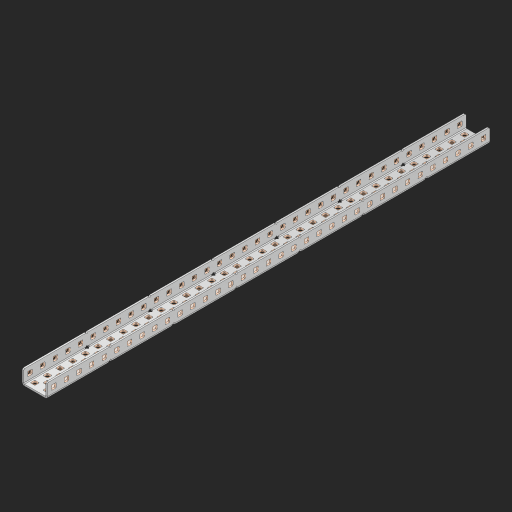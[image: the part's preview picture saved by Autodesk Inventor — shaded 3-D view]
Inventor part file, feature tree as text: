
AUTODESK INVENTOR PART (.ipt)
format: ipt  version: 2023 (Build 270158000, 158)  size: 2,018,816 bytes
history: native  units: in
note: dims shown in document units (in); Inventor stores cm internally (conversion verified against a paired STEP export)
features: other x322, extrude x172, sheet_metal_op x11, sketch x10, pattern_linear x2, mirror x1, chamfer x1
ambient origin geometry x8: Origin, YZ Plane, XZ Plane, XY Plane, X Axis, Y Axis, Z Axis, Center Point
bodies: Solid1 (feature_tree), Body (feature_tree)
feature tree (519):
  other  "Table"
  other  "Alu C 1x2x1x35"
  other  "Alu C 1x2x1x34"
  other  "Alu C 1x2x1x33"
  other  "Alu C 1x2x1x32"
  other  "Alu C 1x2x1x31"
  other  "Alu C 1x2x1x30"
  other  "Alu C 1x2x1x29"
  other  "Alu C 1x2x1x28"
  other  "Alu C 1x2x1x27"
  other  "Alu C 1x2x1x26"
  other  "Alu C 1x2x1x25"
  other  "Alu C 1x2x1x24"
  other  "Alu C 1x2x1x23"
  other  "Alu C 1x2x1x22"
  other  "Alu C 1x2x1x21"
  other  "Alu C 1x2x1x20"
  other  "Alu C 1x2x1x19"
  other  "Alu C 1x2x1x18"
  other  "Alu C 1x2x1x17"
  other  "Alu C 1x2x1x16"
  other  "Alu C 1x2x1x15"
  other  "Alu C 1x2x1x14"
  other  "Alu C 1x2x1x13"
  other  "Alu C 1x2x1x12"
  other  "Alu C 1x2x1x11"
  other  "Alu C 1x2x1x10"
  other  "Alu C 1x2x1x9"
  other  "Alu C 1x2x1x8"
  other  "Alu C 1x2x1x7"
  other  "Alu C 1x2x1x6"
  other  "Alu C 1x2x1x5"
  other  "Alu C 1x2x1x4"
  other  "Alu C 1x2x1x3"
  other  "Alu C 1x2x1x2"
  other  "Alu C 1x2x1x1"
  other  "Steel C 1x2x1x35"
  other  "Steel C 1x2x1x34"
  other  "Steel C 1x2x1x33"
  other  "Steel C 1x2x1x32"
  other  "Steel C 1x2x1x31"
  other  "Steel C 1x2x1x30"
  other  "Steel C 1x2x1x29"
  other  "Steel C 1x2x1x28"
  other  "Steel C 1x2x1x27"
  other  "Steel C 1x2x1x26"
  other  "Steel C 1x2x1x25"
  other  "Steel C 1x2x1x24"
  other  "Steel C 1x2x1x23"
  other  "Steel C 1x2x1x22"
  other  "Steel C 1x2x1x21"
  other  "Steel C 1x2x1x20"
  other  "Steel C 1x2x1x19"
  other  "Steel C 1x2x1x18"
  other  "Steel C 1x2x1x17"
  other  "Steel C 1x2x1x16"
  other  "Steel C 1x2x1x15"
  other  "Steel C 1x2x1x14"
  other  "Steel C 1x2x1x13"
  other  "Steel C 1x2x1x12"
  other  "Steel C 1x2x1x11"
  other  "Steel C 1x2x1x10"
  other  "Steel C 1x2x1x9"
  other  "Steel C 1x2x1x8"
  other  "Steel C 1x2x1x7"
  other  "Steel C 1x2x1x6"
  other  "Steel C 1x2x1x5"
  other  "Steel C 1x2x1x4"
  other  "Steel C 1x2x1x3"
  other  "Steel C 1x2x1x2"
  other  "Steel C 1x2x1x1"
  other  "Alu Half C 1x2x1x35"
  other  "Alu Half C 1x2x1x34"
  other  "Alu Half C 1x2x1x33"
  other  "Alu Half C 1x2x1x32"
  other  "Alu Half C 1x2x1x31"
  other  "Alu Half C 1x2x1x30"
  other  "Alu Half C 1x2x1x29"
  other  "Alu Half C 1x2x1x28"
  other  "Alu Half C 1x2x1x27"
  other  "Alu Half C 1x2x1x26"
  other  "Alu Half C 1x2x1x25"
  other  "Alu Half C 1x2x1x24"
  other  "Alu Half C 1x2x1x23"
  other  "Alu Half C 1x2x1x22"
  other  "Alu Half C 1x2x1x21"
  other  "Alu Half C 1x2x1x20"
  other  "Alu Half C 1x2x1x19"
  other  "Alu Half C 1x2x1x18"
  other  "Alu Half C 1x2x1x17"
  other  "Alu Half C 1x2x1x16"
  other  "Alu Half C 1x2x1x15"
  other  "Alu Half C 1x2x1x14"
  other  "Alu Half C 1x2x1x13"
  other  "Alu Half C 1x2x1x12"
  other  "Alu Half C 1x2x1x11"
  other  "Alu Half C 1x2x1x10"
  other  "Alu Half C 1x2x1x9"
  other  "Alu Half C 1x2x1x8"
  other  "Alu Half C 1x2x1x7"
  other  "Alu Half C 1x2x1x6"
  other  "Alu Half C 1x2x1x5"
  other  "Alu Half C 1x2x1x4"
  other  "Alu Half C 1x2x1x3"
  other  "Alu Half C 1x2x1x2"
  other  "Alu Half C 1x2x1x1"
  other  "Steel Half C 1x2x1x35"
  other  "Steel Half C 1x2x1x34"
  other  "Steel Half C 1x2x1x33"
  other  "Steel Half C 1x2x1x32"
  other  "Steel Half C 1x2x1x31"
  other  "Steel Half C 1x2x1x30"
  other  "Steel Half C 1x2x1x29"
  other  "Steel Half C 1x2x1x28"
  other  "Steel Half C 1x2x1x27"
  other  "Steel Half C 1x2x1x26"
  other  "Steel Half C 1x2x1x25"
  other  "Steel Half C 1x2x1x24"
  other  "Steel Half C 1x2x1x23"
  other  "Steel Half C 1x2x1x22"
  other  "Steel Half C 1x2x1x21"
  other  "Steel Half C 1x2x1x20"
  other  "Steel Half C 1x2x1x19"
  other  "Steel Half C 1x2x1x18"
  other  "Steel Half C 1x2x1x17"
  other  "Steel Half C 1x2x1x16"
  other  "Steel Half C 1x2x1x15"
  other  "Steel Half C 1x2x1x14"
  other  "Steel Half C 1x2x1x13"
  other  "Steel Half C 1x2x1x12"
  other  "Steel Half C 1x2x1x11"
  other  "Steel Half C 1x2x1x10"
  other  "Steel Half C 1x2x1x9"
  other  "Steel Half C 1x2x1x8"
  other  "Steel Half C 1x2x1x7"
  other  "Steel Half C 1x2x1x6"
  other  "Steel Half C 1x2x1x5"
  other  "Steel Half C 1x2x1x4"
  other  "Steel Half C 1x2x1x3"
  other  "Steel Half C 1x2x1x2"
  other  "Steel Half C 1x2x1x1"
  sheet_metal_op  "Flanges"
  other  "Flange Pattern Plane"
  other  "Flange Pattern Sketch"
  sheet_metal_op  "Flange Pattern"
  sheet_metal_op  "Body Pattern"
  pattern_linear  "Center Pattern"  Spacing1=0.0625in  [1 undecoded]
  other  "Arc Length"
  mirror  "Notch Mirror"
  pattern_linear  "Notch Pattern"  Spacing1=0.182in  [1 undecoded]
  chamfer  "End Chamfer"
  extrude  "Half Cut"  Depth=0.02in
  sketch  "Sketch1"  dims[d0=1.0in]
  other  "Plate1"
  sketch  "Sketch2"  dims[d1=17.5in]
  other  "Plate2"
  sheet_metal_op  "Bend1"
  sheet_metal_op  "Corner1"
  sketch  "Sketch3"  dims[d2=0.0625in]
  sketch  "Sketch7"  dims[d3=0.0625in]
  other  "Srf1"
  other  "Srf2"
  sketch  "Sketch8"  dims[d4=0.0312in]
  sketch  "Sketch9"  dims[d5=0.125in]
  other  "Srf91"
  sheet_metal_op  "Body Pattern Sketch"
  other  "Srf92"
  sketch  "Sketch13"  dims[d6=0.0625in]
  sketch  "Sketch14"  dims[d7=0.5in d8=90.0deg d9=0.0312in]
  sketch  "Sketch15"  dims[d10=0.25in]
  sketch  "Sketch16"  dims[d11=0.0625in d12=0.0625in d16=0.182in d17=0.02in d18=0.0625in d19=0.0in d20=0.25in d21=0.25in d38=13.7795in d40=0.5in d41=0.7874in d43=1.0in d46=0.172in d47=1.0in d48=0.0in d49=0.182in d50=0.02in d51=0.25in d52=0.25in d53=0.0625in d54=0.0in d55=0.172in d56=1.0in d57=0.0in d58=0.25in d60=13.7795in d62=0.5in d63=0.7874in d65=0.5in d85=0.1473in d86=0.1782in d88=0.04in d89=0.0625in d90=0.0in d91=0.04in d92=0.0491in d95=2.5in d96=0.04in d97=0.25in d98=45.0deg d99=0.25in d100=0.5in d101=0.0in d102=2.497in d106=0.182in d107=0.02in d108=0.5in d109=0.5in d110=0.0625in d111=0.0in d112=0.172in d113=0.5in d114=0.0in d117=0.5in d118=0.5in d119=0.5in]
  other  "Srf786"
  other  "Srf823"
  other  "Srf824"
  other  "Srf825"
  other  "Srf826"
  other  "Srf827"
  other  "Srf828"
  other  "Srf829"
  other  "Srf856"
  other  "Srf857"
  other  "Srf858"
  other  "Srf859"
  other  "Srf860"
  other  "Srf861"
  other  "Srf862"
  other  "Srf889"
  other  "Srf890"
  other  "Srf891"
  other  "Srf892"
  other  "Srf893"
  other  "Srf894"
  other  "Srf895"
  other  "Srf896"
  other  "Srf922"
  other  "Srf923"
  other  "Srf924"
  other  "Srf925"
  other  "Srf926"
  other  "Srf959"
  other  "Srf960"
  other  "Srf961"
  other  "Srf962"
  other  "Srf963"
  other  "Srf996"
  other  "Srf997"
  other  "Srf998"
  other  "Srf999"
  other  "Srf1000"
  other  "Srf1143"
  other  "Srf1144"
  other  "Srf1145"
  other  "Srf1146"
  other  "Srf1147"
  other  "Srf1148"
  other  "Srf1149"
  other  "Srf1150"
  other  "Srf1151"
  other  "Srf1152"
  other  "Srf1153"
  other  "Srf1154"
  other  "Srf1155"
  other  "Srf1156"
  other  "Srf1157"
  other  "Srf1158"
  other  "Srf1159"
  other  "Srf1160"
  other  "Srf1161"
  other  "Srf1162"
  other  "Srf1163"
  other  "Srf1164"
  other  "Srf1165"
  other  "Srf1166"
  other  "Srf1167"
  other  "Srf1168"
  other  "Srf1169"
  other  "Srf1170"
  other  "Srf1171"
  other  "Srf1172"
  other  "Srf1173"
  other  "Srf1174"
  other  "Srf1175"
  other  "Srf1176"
  other  "Srf1177"
  other  "Srf1178"
  other  "Srf1179"
  other  "Srf1180"
  other  "Srf1181"
  other  "Srf1182"
  other  "Srf1183"
  other  "Srf1184"
  other  "Srf1185"
  other  "Srf1186"
  other  "Srf1187"
  other  "Srf1188"
  other  "Srf1189"
  other  "Srf1190"
  other  "Srf1191"
  other  "Srf1192"
  other  "Srf1193"
  other  "Srf1194"
  other  "Srf1195"
  other  "Srf1196"
  other  "Srf1197"
  other  "Srf1198"
  other  "Srf1199"
  other  "Srf1200"
  other  "Srf1201"
  other  "Srf1202"
  other  "Srf1203"
  other  "Srf1204"
  other  "Srf1205"
  other  "Srf1206"
  other  "Srf1207"
  other  "Srf1208"
  other  "Srf1209"
  other  "Srf1210"
  other  "Srf1211"
  other  "Srf1212"
  other  "Srf1213"
  other  "Srf1214"
  other  "Srf1215"
  other  "Srf1216"
  other  "Srf1217"
  other  "Srf1218"
  other  "Srf1219"
  other  "Srf1220"
  other  "Srf1221"
  other  "Srf1222"
  other  "Srf1223"
  other  "Srf1224"
  other  "Srf1225"
  other  "Srf1226"
  other  "Srf1227"
  other  "Srf1228"
  other  "Srf1229"
  other  "Srf1230"
  other  "Srf1231"
  other  "Srf1232"
  other  "Srf1233"
  other  "Srf1234"
  other  "Srf1235"
  other  "Srf1236"
  other  "Srf1237"
  other  "Srf1238"
  other  "Srf1239"
  other  "Srf1240"
  other  "Srf1241"
  other  "Srf1242"
  other  "Srf1243"
  other  "Srf1244"
  other  "Srf1245"
  other  "Srf1246"
  other  "Srf1247"
  other  "Srf1248"
  other  "Srf1249"
  other  "Srf1250"
  other  "Srf1251"
  other  "Srf1252"
  other  "Srf1253"
  other  "Srf1254"
  other  "Srf1255"
  other  "Srf1256"
  other  "Srf1257"
  other  "Srf1258"
  other  "Srf1259"
  other  "Srf1260"
  other  "Srf1261"
  other  "Srf1262"
  other  "Srf1263"
  other  "Srf1264"
  other  "Srf1265"
  other  "Srf1266"
  other  "Srf1267"
  other  "Srf1268"
  other  "Srf1269"
  other  "Srf1270"
  other  "Srf1271"
  other  "Srf1272"
  other  "Srf1273"
  other  "Srf1274"
  sheet_metal_op  "Flange Stamp"
  sheet_metal_op  "Flange Circle"
  sheet_metal_op  "Body Stamp"
  sheet_metal_op  "Body Circle"
  other  "Center Stamp"
  other  "Center Circle"
  sheet_metal_op  "Notch"
  extrude  "ExtrusionSrf2"  Depth=0.0625in
  extrude  "ExtrusionSrf92"  TaperAngle=0.0deg  [1 undecoded]
  extrude  "ExtrusionSrf823"  Depth=0.5in
  extrude  "ExtrusionSrf824"  Depth=0.5in
  extrude  "ExtrusionSrf825"  Depth=0.5in
  extrude  "ExtrusionSrf826"  Depth=0.5in
  extrude  "ExtrusionSrf827"  Depth=1.0in TaperAngle=0.0deg
  extrude  "ExtrusionSrf828"  Depth=0.5in
  extrude  "ExtrusionSrf829"  Depth=0.02in
  extrude  "ExtrusionSrf856"  Depth=0.5in
  extrude  "ExtrusionSrf857"  Depth=0.5in
  extrude  "ExtrusionSrf858"  Depth=0.0625in
  extrude  "ExtrusionSrf859"  TaperAngle=0.0deg  [1 undecoded]
  extrude  "ExtrusionSrf860"  Depth=0.5in
  extrude  "ExtrusionSrf861"  Depth=1.0in TaperAngle=0.0deg
  extrude  "ExtrusionSrf862"  Depth=0.5in
  extrude  "ExtrusionSrf889"  Depth=0.5in
  extrude  "ExtrusionSrf890"  Depth=0.5in
  extrude  "ExtrusionSrf891"  Depth=0.5in
  extrude  "ExtrusionSrf892"  Depth=0.5in
  extrude  "ExtrusionSrf893"  Depth=0.5in
  extrude  "ExtrusionSrf894"  Depth=0.0625in
  extrude  "ExtrusionSrf895"  TaperAngle=0.0deg  [1 undecoded]
  extrude  "ExtrusionSrf896"  Depth=0.5in
  extrude  "ExtrusionSrf922"  Depth=0.5in
  extrude  "ExtrusionSrf923"  Depth=2.5in
  extrude  "ExtrusionSrf924"  Depth=0.5in TaperAngle=45.0deg
  extrude  "ExtrusionSrf925"  Depth=0.5in
  extrude  "ExtrusionSrf926"  Depth=0.5in TaperAngle=0.0deg
  extrude  "ExtrusionSrf959"  Depth=0.5in
  extrude  "ExtrusionSrf960"  Depth=0.5in
  extrude  "ExtrusionSrf961"  Depth=0.02in
  extrude  "ExtrusionSrf962"  Depth=0.5in
  extrude  "ExtrusionSrf963"  Depth=0.5in
  extrude  "ExtrusionSrf996"  Depth=0.0625in
  extrude  "ExtrusionSrf997"  TaperAngle=0.0deg  [1 undecoded]
  extrude  "ExtrusionSrf998"  Depth=0.5in
  extrude  "ExtrusionSrf999"  Depth=0.5in TaperAngle=0.0deg
  extrude  "ExtrusionSrf1000"  Depth=0.5in
  extrude  "ExtrusionSrf1143"  Depth=0.5in
  extrude  "ExtrusionSrf1144"  Depth=0.5in
  extrude  "ExtrusionSrf1145"  [1 undecoded]
  extrude  "ExtrusionSrf1146"  [1 undecoded]
  extrude  "ExtrusionSrf1147"  [1 undecoded]
  extrude  "ExtrusionSrf1148"  [1 undecoded]
  extrude  "ExtrusionSrf1149"  [1 undecoded]
  extrude  "ExtrusionSrf1150"  [1 undecoded]
  extrude  "ExtrusionSrf1151"  [1 undecoded]
  extrude  "ExtrusionSrf1152"  [1 undecoded]
  extrude  "ExtrusionSrf1153"  [1 undecoded]
  extrude  "ExtrusionSrf1154"  [1 undecoded]
  extrude  "ExtrusionSrf1155"  [1 undecoded]
  extrude  "ExtrusionSrf1156"  [1 undecoded]
  extrude  "ExtrusionSrf1157"  [1 undecoded]
  extrude  "ExtrusionSrf1158"  [1 undecoded]
  extrude  "ExtrusionSrf1159"  [1 undecoded]
  extrude  "ExtrusionSrf1160"  [1 undecoded]
  extrude  "ExtrusionSrf1161"  [1 undecoded]
  extrude  "ExtrusionSrf1162"  [1 undecoded]
  extrude  "ExtrusionSrf1163"  [1 undecoded]
  extrude  "ExtrusionSrf1164"  [1 undecoded]
  extrude  "ExtrusionSrf1165"  [1 undecoded]
  extrude  "ExtrusionSrf1166"  [1 undecoded]
  extrude  "ExtrusionSrf1167"  [1 undecoded]
  extrude  "ExtrusionSrf1168"  [1 undecoded]
  extrude  "ExtrusionSrf1169"  [1 undecoded]
  extrude  "ExtrusionSrf1170"  [1 undecoded]
  extrude  "ExtrusionSrf1171"  [1 undecoded]
  extrude  "ExtrusionSrf1172"  [1 undecoded]
  extrude  "ExtrusionSrf1173"  [1 undecoded]
  extrude  "ExtrusionSrf1174"  [1 undecoded]
  extrude  "ExtrusionSrf1175"  [1 undecoded]
  extrude  "ExtrusionSrf1176"  [1 undecoded]
  extrude  "ExtrusionSrf1177"  [1 undecoded]
  extrude  "ExtrusionSrf1178"  [1 undecoded]
  extrude  "ExtrusionSrf1179"  [1 undecoded]
  extrude  "ExtrusionSrf1180"  [1 undecoded]
  extrude  "ExtrusionSrf1181"  [1 undecoded]
  extrude  "ExtrusionSrf1182"  [1 undecoded]
  extrude  "ExtrusionSrf1183"  [1 undecoded]
  extrude  "ExtrusionSrf1184"  [1 undecoded]
  extrude  "ExtrusionSrf1185"  [1 undecoded]
  extrude  "ExtrusionSrf1186"  [1 undecoded]
  extrude  "ExtrusionSrf1187"  [1 undecoded]
  extrude  "ExtrusionSrf1188"  [1 undecoded]
  extrude  "ExtrusionSrf1189"  [1 undecoded]
  extrude  "ExtrusionSrf1190"  [1 undecoded]
  extrude  "ExtrusionSrf1191"  [1 undecoded]
  extrude  "ExtrusionSrf1192"  [1 undecoded]
  extrude  "ExtrusionSrf1193"  [1 undecoded]
  extrude  "ExtrusionSrf1194"  [1 undecoded]
  extrude  "ExtrusionSrf1195"  [1 undecoded]
  extrude  "ExtrusionSrf1196"  [1 undecoded]
  extrude  "ExtrusionSrf1197"  [1 undecoded]
  extrude  "ExtrusionSrf1198"  [1 undecoded]
  extrude  "ExtrusionSrf1199"  [1 undecoded]
  extrude  "ExtrusionSrf1200"  [1 undecoded]
  extrude  "ExtrusionSrf1201"  [1 undecoded]
  extrude  "ExtrusionSrf1202"  [1 undecoded]
  extrude  "ExtrusionSrf1203"  [1 undecoded]
  extrude  "ExtrusionSrf1204"  [1 undecoded]
  extrude  "ExtrusionSrf1205"  [1 undecoded]
  extrude  "ExtrusionSrf1206"  [1 undecoded]
  extrude  "ExtrusionSrf1207"  [1 undecoded]
  extrude  "ExtrusionSrf1208"  [1 undecoded]
  extrude  "ExtrusionSrf1209"  [1 undecoded]
  extrude  "ExtrusionSrf1210"  [1 undecoded]
  extrude  "ExtrusionSrf1211"  [1 undecoded]
  extrude  "ExtrusionSrf1212"  [1 undecoded]
  extrude  "ExtrusionSrf1213"  [1 undecoded]
  extrude  "ExtrusionSrf1214"  [1 undecoded]
  extrude  "ExtrusionSrf1215"  [1 undecoded]
  extrude  "ExtrusionSrf1216"  [1 undecoded]
  extrude  "ExtrusionSrf1217"  [1 undecoded]
  extrude  "ExtrusionSrf1218"  [1 undecoded]
  extrude  "ExtrusionSrf1219"  [1 undecoded]
  extrude  "ExtrusionSrf1220"  [1 undecoded]
  extrude  "ExtrusionSrf1221"  [1 undecoded]
  extrude  "ExtrusionSrf1222"  [1 undecoded]
  extrude  "ExtrusionSrf1223"  [1 undecoded]
  extrude  "ExtrusionSrf1224"  [1 undecoded]
  extrude  "ExtrusionSrf1225"  [1 undecoded]
  extrude  "ExtrusionSrf1226"  [1 undecoded]
  extrude  "ExtrusionSrf1227"  [1 undecoded]
  extrude  "ExtrusionSrf1228"  [1 undecoded]
  extrude  "ExtrusionSrf1229"  [1 undecoded]
  extrude  "ExtrusionSrf1230"  [1 undecoded]
  extrude  "ExtrusionSrf1231"  [1 undecoded]
  extrude  "ExtrusionSrf1232"  [1 undecoded]
  extrude  "ExtrusionSrf1233"  [1 undecoded]
  extrude  "ExtrusionSrf1234"  [1 undecoded]
  extrude  "ExtrusionSrf1235"  [1 undecoded]
  extrude  "ExtrusionSrf1236"  [1 undecoded]
  extrude  "ExtrusionSrf1237"  [1 undecoded]
  extrude  "ExtrusionSrf1238"  [1 undecoded]
  extrude  "ExtrusionSrf1239"  [1 undecoded]
  extrude  "ExtrusionSrf1240"  [1 undecoded]
  extrude  "ExtrusionSrf1241"  [1 undecoded]
  extrude  "ExtrusionSrf1242"  [1 undecoded]
  extrude  "ExtrusionSrf1243"  [1 undecoded]
  extrude  "ExtrusionSrf1244"  [1 undecoded]
  extrude  "ExtrusionSrf1245"  [1 undecoded]
  extrude  "ExtrusionSrf1246"  [1 undecoded]
  extrude  "ExtrusionSrf1247"  [1 undecoded]
  extrude  "ExtrusionSrf1248"  [1 undecoded]
  extrude  "ExtrusionSrf1249"  [1 undecoded]
  extrude  "ExtrusionSrf1250"  [1 undecoded]
  extrude  "ExtrusionSrf1251"  [1 undecoded]
  extrude  "ExtrusionSrf1252"  [1 undecoded]
  extrude  "ExtrusionSrf1253"  [1 undecoded]
  extrude  "ExtrusionSrf1254"  [1 undecoded]
  extrude  "ExtrusionSrf1255"  [1 undecoded]
  extrude  "ExtrusionSrf1256"  [1 undecoded]
  extrude  "ExtrusionSrf1257"  [1 undecoded]
  extrude  "ExtrusionSrf1258"  [1 undecoded]
  extrude  "ExtrusionSrf1259"  [1 undecoded]
  extrude  "ExtrusionSrf1260"  [1 undecoded]
  extrude  "ExtrusionSrf1261"  [1 undecoded]
  extrude  "ExtrusionSrf1262"  [1 undecoded]
  extrude  "ExtrusionSrf1263"  [1 undecoded]
  extrude  "ExtrusionSrf1264"  [1 undecoded]
  extrude  "ExtrusionSrf1265"  [1 undecoded]
  extrude  "ExtrusionSrf1266"  [1 undecoded]
  extrude  "ExtrusionSrf1267"  [1 undecoded]
  extrude  "ExtrusionSrf1268"  [1 undecoded]
  extrude  "ExtrusionSrf1269"  [1 undecoded]
  extrude  "ExtrusionSrf1270"  [1 undecoded]
  extrude  "ExtrusionSrf1271"  [1 undecoded]
  extrude  "ExtrusionSrf1272"  [1 undecoded]
  extrude  "ExtrusionSrf1273"  [1 undecoded]
  extrude  "ExtrusionSrf1274"  [1 undecoded]
note: 136 required parameter values undecoded (feature->parameter linkage not recoverable at this tier; creation-order binding heuristic only, values carry confidence <= 0.55)
